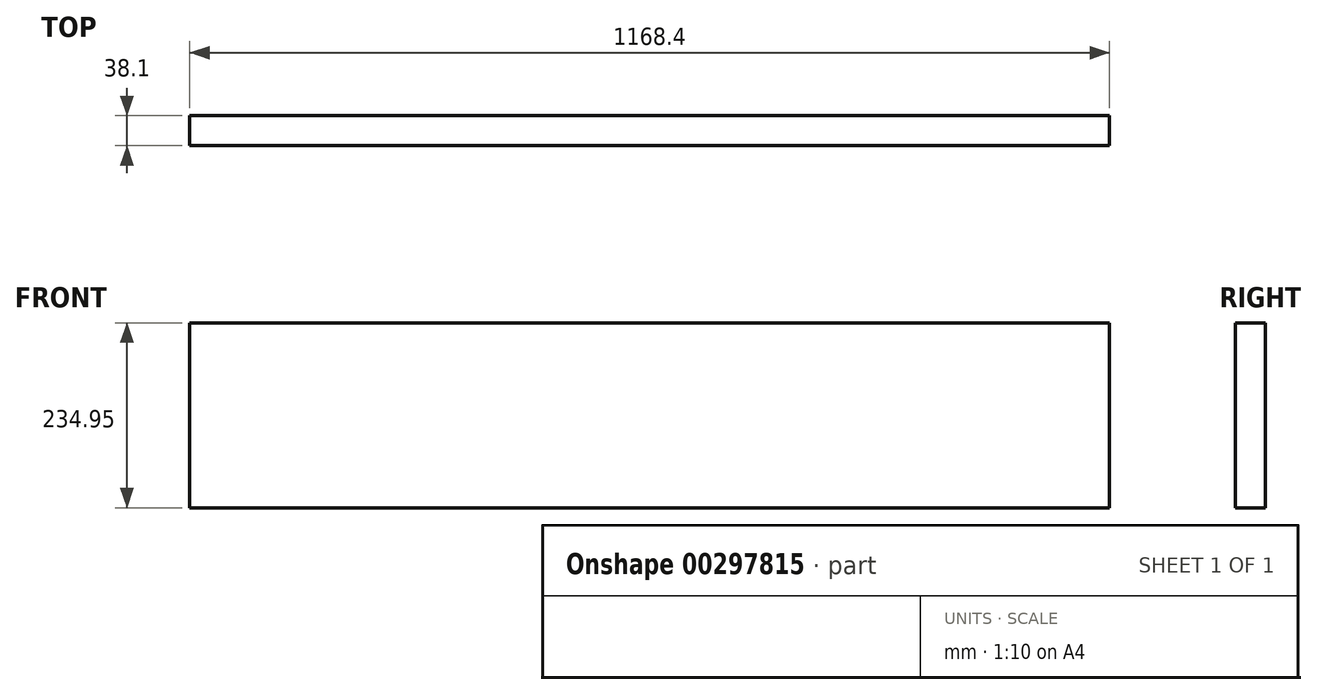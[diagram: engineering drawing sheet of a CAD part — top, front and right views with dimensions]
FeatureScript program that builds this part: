
annotation { "Feature Type Name" : "Feature", "Feature Type Description" : "" }
export const myFeature = defineFeature(function(context is Context, id is Id, definition is map)
    precondition{}
    {
        {
            var Q0;
            Q0=qCreatedBy(makeId("Front.planeOp"),FACE);
            var sketch = newSketch(context, id + "F0", { "sketchPlane" : qUnion([Q0])});
            skLineSegment(sketch, "E0.bottom", {"start": v(0, 0) * mm, "end": v(1168.4, 0) * mm});
            skLineSegment(sketch, "E0.top", {"start": v(0, 234.95) * mm, "end": v(1168.4, 234.95) * mm});
            skLineSegment(sketch, "E0.left", {"start": v(0, 0) * mm, "end": v(0, 234.95) * mm});
            skLineSegment(sketch, "E0.right", {"start": v(1168.4, 0) * mm, "end": v(1168.4, 234.95) * mm});
            skSolve(sketch);
        }
        {
            var Q0;
            Q0=makeQuery(id+"F0.imprint","IMPRINT",FACE,{"disambiguationData":[TD([[makeQuery(id+"F0.imprint","IMPRINT",EDGE,{"derivedFrom":sQuery(id+"F0.wireOp",EDGE,"E0.bottom")}),1.0]])]});
            extrude(context, id + "F1", {"entities" : qUnion([Q0]), "depth" : 38.1 * mm});
        }
    });
